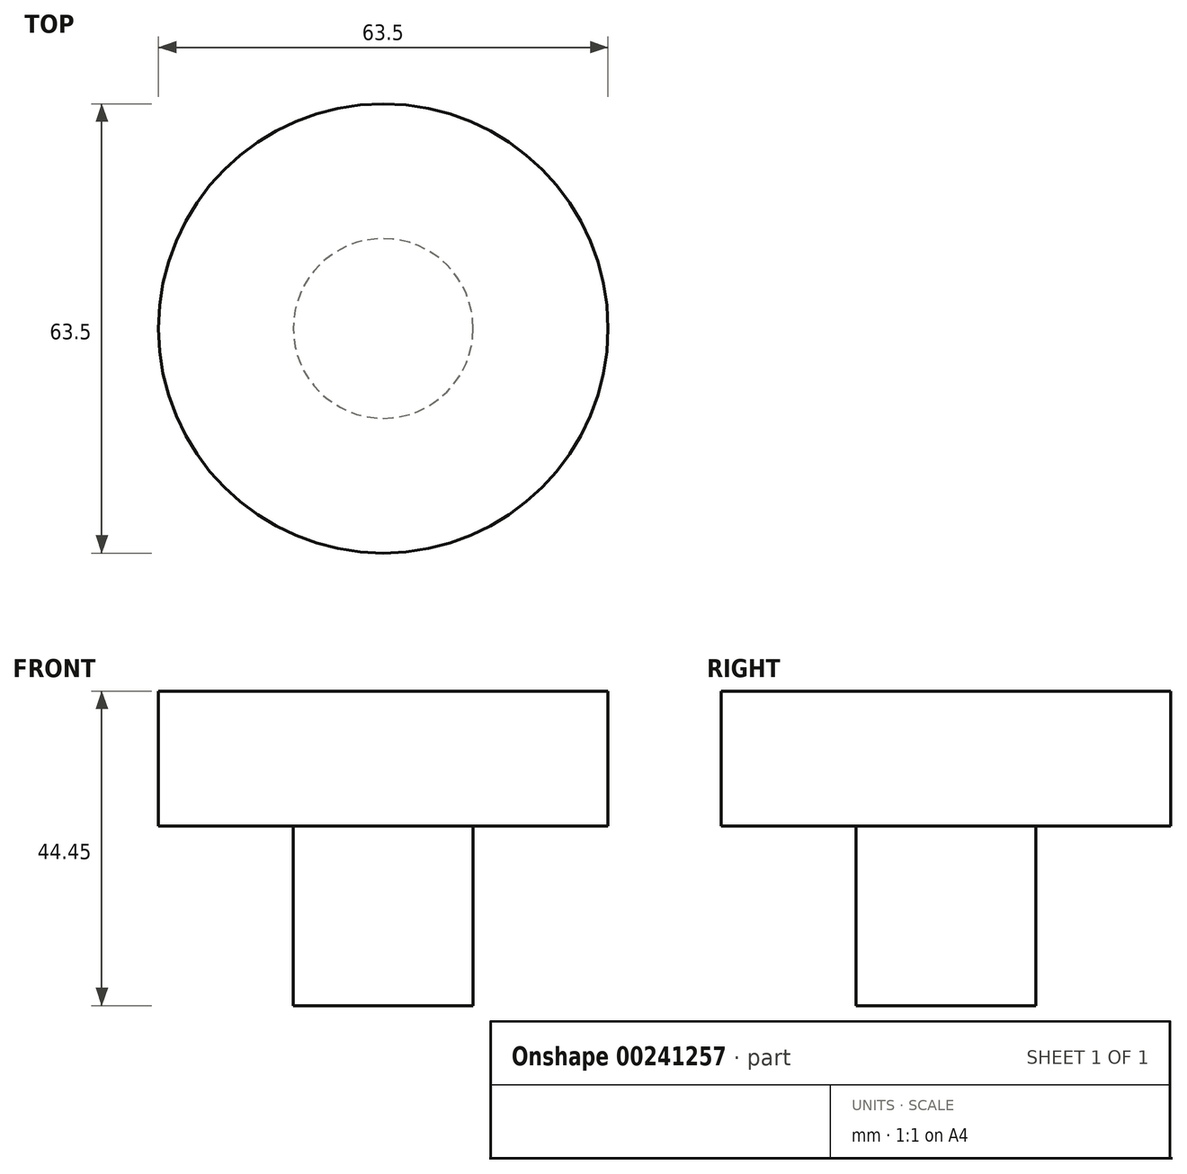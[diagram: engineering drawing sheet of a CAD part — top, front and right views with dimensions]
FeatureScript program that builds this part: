
annotation { "Feature Type Name" : "Feature", "Feature Type Description" : "" }
export const myFeature = defineFeature(function(context is Context, id is Id, definition is map)
    precondition{}
    {
        {
            var Q0;
            Q0=qCreatedBy(makeId("Front.planeOp"),FACE);
            var sketch = newSketch(context, id + "F0", { "sketchPlane" : qUnion([Q0])});
            skLineSegment(sketch, "E0", {"start": v(0, 57.07) * mm, "end": v(0, -23.78) * mm, "construction": true});
            skLineSegment(sketch, "E1", {"start": v(0, 0) * mm, "end": v(-12.7, 0) * mm, "construction": true});
            skLineSegment(sketch, "E2", {"start": v(-12.7, 0) * mm, "end": v(-12.7, 25.4) * mm, "construction": true});
            skLineSegment(sketch, "E3", {"start": v(-12.7, 25.4) * mm, "end": v(-12.7, 0) * mm});
            skLineSegment(sketch, "E4", {"start": v(0, 0) * mm, "end": v(-12.7, 0) * mm});
            skLineSegment(sketch, "E5", {"start": v(-12.7, 25.4) * mm, "end": v(-31.75, 25.4) * mm});
            skLineSegment(sketch, "E6", {"start": v(-31.75, 25.4) * mm, "end": v(-31.75, 44.45) * mm});
            skLineSegment(sketch, "E7", {"start": v(-31.75, 44.45) * mm, "end": v(0, 44.45) * mm});
            skLineSegment(sketch, "E8", {"start": v(0, 44.45) * mm, "end": v(0, 0) * mm});
            skSolve(sketch);
        }
        {
            var Q0;
            Q0=makeQuery(id+"F0.imprint","IMPRINT",FACE,{"disambiguationData":[TD([[makeQuery(id+"F0.imprint","IMPRINT",EDGE,{"derivedFrom":sQuery(id+"F0.wireOp",EDGE,"E3")}),1.0]])]});
            var Q1;
            Q1=sQuery(id+"F0.wireOp",EDGE,"E0");
            revolve(context, id + "F1", {"entities" : qUnion([Q0]), "axis" : qUnion([Q1]), "revolveType" : RevolveType.FULL});
        }
    });
